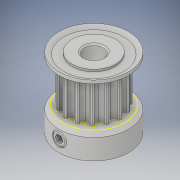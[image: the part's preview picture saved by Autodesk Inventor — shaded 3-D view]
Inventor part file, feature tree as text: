
AUTODESK INVENTOR PART (.ipt)
format: ipt  version: 2019.2 (Build 232265000, 265)  size: 492,032 bytes
history: native  units: mm
features: move_body x2, other x1, sketch x1, imported_body x1
ambient origin geometry x8: Origin, YZ Plane, XZ Plane, XY Plane, X Axis, Y Axis, Z Axis, Center Point
bodies: Solid1 (feature_tree)
feature tree (5):
  other  "gates_P15-3M-09AL.stp"
  move_body  "Move Body1"
  move_body  "Move Body2"
  sketch  "Sketch2"  dims[d0=90.0deg d1=-15.707963mm]
  imported_body  "Base1"
